SOLIDWORKS PART (.sldprt)
format: sldprt  version: not decoded by parser v0  size: 794,112 bytes
history: native  units: mm
features: sketch x20, cut_extrude x16, chamfer x6, plane x4, extrude x4, mirror x3, material x1 (+8 scaffold rows collapsed)
feature tree (62):
  scaffold x8  (default folders/planes/origin — collapsed)
  material  "Material <not specified>"
  plane  "Alzado"
  plane  "Planta"
  plane  "Vista lateral"
  sketch  "Croquis1"  dims[D1=23.5mm D2=35.0mm D3=6.7mm D4=2.9mm]
  extrude  "Extruir1"  Depth=9.9mm
  sketch  "Croquis2"  dims[c1.D1=2.0mm c1.D2=2.0mm c2.D1=~2.838727mm c2.D2=~3.245594mm c2.D3=3.0mm c2.D4=40.16mm c2.D5=20.08mm]
  cut_extrude  "Cortar-Extruir1"  Depth=15.9mm
  sketch  "Croquis3"
  cut_extrude  "Cortar-Extruir2"  Depth=4mm
  sketch  "Croquis4"  dims[D1=35.0mm D2=17.5mm D3=1.5mm]
  cut_extrude  "Cortar-Extruir3"  Depth=24mm
  sketch  "Croquis5"  dims[D1=2.0mm]
  cut_extrude  "Cortar-Extruir4"  Depth=8.5mm
  sketch  "Croquis6"  dims[D1=39.0mm D2=19.5mm]
  cut_extrude  "Cortar-Extruir5"  Depth=3mm
  plane  "Plano1"  Offset=6mm
  sketch  "Croquis7"  dims[D4=4.0mm D1=6.0mm D2=4.0mm D3=4.5mm]
  extrude  "Extruir2"  Depth=0.2mm
  sketch  "Croquis8"  dims[D1=21.5mm]
  cut_extrude  "Cortar-Extruir6"  Depth=0.5mm
  sketch  "Croquis9"  dims[D1=1.5mm D2=14.0mm D3=18.0mm]
  cut_extrude  "Cortar-Extruir7"  Depth=1mm
  chamfer  "Chaflán1"  Distance=0.5mm Angle=45deg
  chamfer  "Chaflán2"  Distance=0.5mm Angle=45deg
  sketch  "Croquis10"  dims[D1=32.2mm D2=2.9mm D3=16.1mm]
  extrude  "Extruir3"  [1 undecoded]
  sketch  "Croquis11"  dims[D1=0.7mm D2=0.7mm D3=0.7mm D4=10.5mm]
  cut_extrude  "Cortar-Extruir8"  Depth=2.5mm
  sketch  "Croquis12"  dims[D1=7.5mm D2=23.5mm D3=2.0mm]
  cut_extrude  "Cortar-Extruir9"  Depth=57.5mm
  sketch  "Croquis13"  dims[D1=2.0mm]
  cut_extrude  "Cortar-Extruir10"  Depth=0.7mm
  sketch  "Croquis15"  dims[D1=4.0mm D2=19.0mm D3=2.0mm D4=5.5mm]
  extrude  "Extruir4"  Depth=0.5mm
  chamfer  "Chaflán3"  Distance=0.5mm Angle=45deg
  sketch  "Croquis16"  dims[D1=3.0mm D2=6.5mm]
  cut_extrude  "Cortar-Extruir11"  Depth=1mm
  mirror  "Simetría1"
  chamfer  "Chaflán4"  Distance=0.5mm Angle=45deg
  sketch  "Croquis17"  dims[D1=27.8mm D2=27.8mm D3=2.0mm D4=1.5mm D5=1.25mm D6=15.0mm]
  cut_extrude  "Cortar-Extruir12"  Depth=1mm
  chamfer  "Chaflán5"  Distance=0.5mm Angle=45deg
  mirror  "Simetría2"
  chamfer  "Chaflán6"  Distance=0.5mm Angle=45deg
  sketch  "Croquis18"  dims[D1=1.6mm]
  cut_extrude  "Cortar-Extruir13"  Depth=22mm
  sketch  "Croquis19"  dims[D1=0.6mm D2=0.6mm]
  cut_extrude  "Cortar-Extruir14"  Depth=0.2mm
  sketch  "Croquis20"  dims[D1=2.0mm]
  cut_extrude  "Cortar-Extruir15"  Depth=0.2mm
  mirror  "Simetría3"  PW2_UID_val=0mm
  sketch  "Croquis21"  dims[D1=8.5mm]
  cut_extrude  "Cortar-Extruir16"  Depth=58mm
decode coverage: 45 of 49 modeling features carry decoded parameters
note: ~ marks probable driven/reference dimensions
note: 1 parameter value undecoded
note: suppression state not decoded; provenance and decode notes live in map.json
